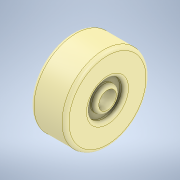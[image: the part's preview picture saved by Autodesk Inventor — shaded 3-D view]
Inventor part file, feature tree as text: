
AUTODESK INVENTOR PART (.ipt)
format: ipt  version: 2022.1 (Build 261234000, 234)  size: 192,512 bytes
history: native  units: mm
features: extrude x4, sketch x4, fillet x3, other x1
ambient origin geometry x8: Origin, YZ Plane, XZ Plane, XY Plane, X Axis, Y Axis, Z Axis, Center Point
bodies: Body1 (feature_tree)
feature tree (12):
  other  "Sólido1"
  extrude  "Extrusión1"  Depth=50.0mm TaperAngle=0.0deg
  sketch  "Boceto2"  dims[d4=5.0mm d5=35.0mm d6=7.5mm d7=0.0mm]
  fillet  "Empalme1"  Radius=50.0mm
  extrude  "Extrusión2"  Depth=35.0mm
  fillet  "Empalme2"  Radius=7.5mm
  extrude  "Extrusión3"  Depth=7.5mm TaperAngle=0.0deg
  fillet  "Empalme3"  Radius=5.0mm
  extrude  "Extrusión4"  Depth=0.872665mm
  sketch  "Boceto1"  dims[d0=120.0mm d1=50.0mm d2=0.0mm d3=50.0mm]
  sketch  "Boceto3"  dims[d8=5.0mm d10=7.5mm d11=0.0mm d12=5.0mm]
  sketch  "Boceto4"  dims[d13=0.0mm d14=0.0mm d9=0.872665mm]
